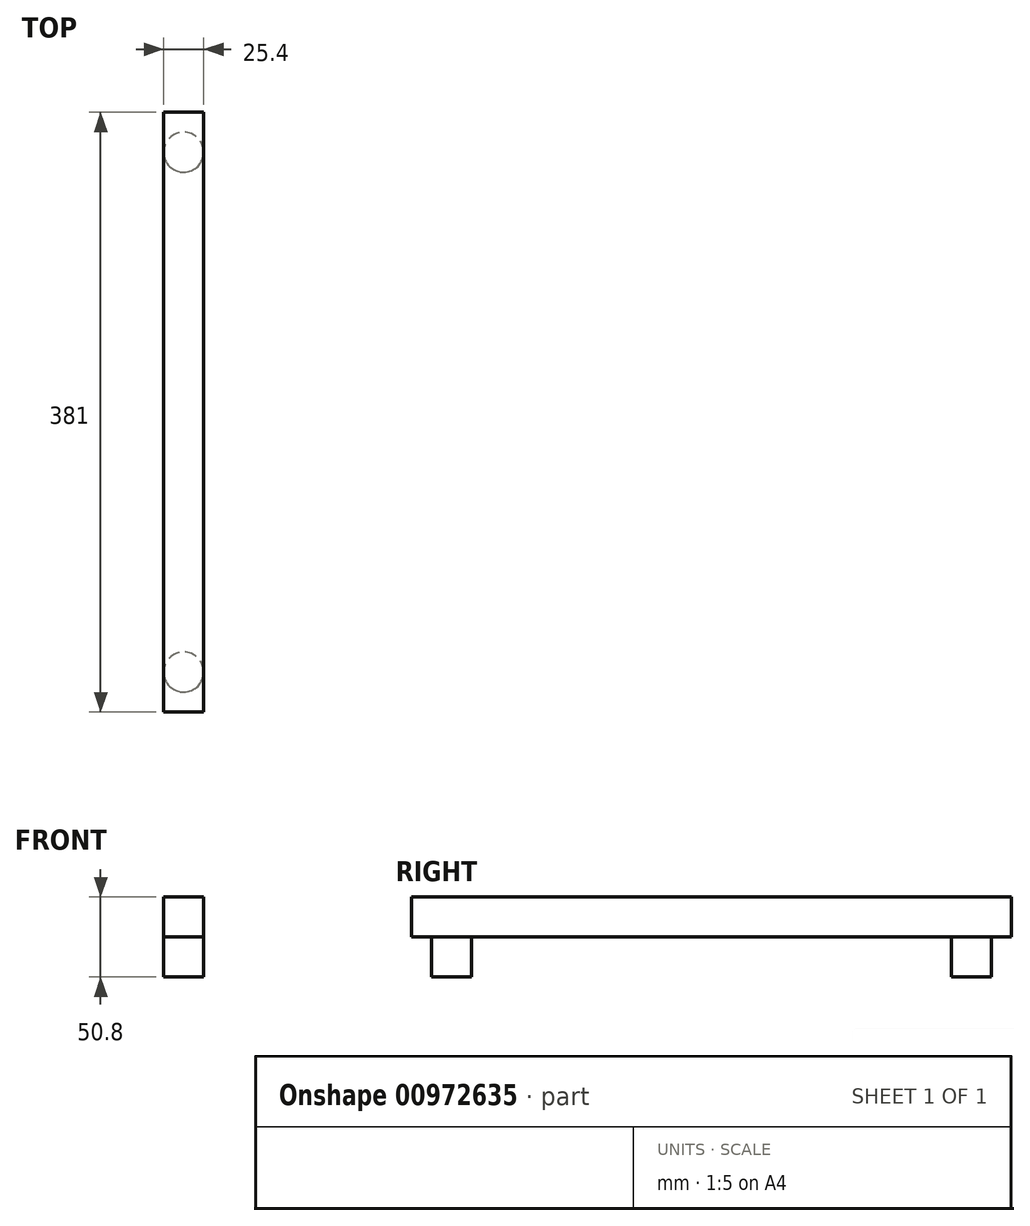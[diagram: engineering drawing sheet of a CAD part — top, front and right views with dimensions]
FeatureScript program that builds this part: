
annotation { "Feature Type Name" : "Feature", "Feature Type Description" : "" }
export const myFeature = defineFeature(function(context is Context, id is Id, definition is map)
    precondition{}
    {
        {
            var Q0;
            Q0=qCreatedBy(makeId("Top.planeOp"),FACE);
            var sketch = newSketch(context, id + "F0", { "sketchPlane" : qUnion([Q0])});
            skCircle(sketch, "E0", {"center": v(-130.07, -20.03) * mm, "radius": 12.7 * mm});
            skSolve(sketch);
        }
        {
            var Q0;
            Q0=makeQuery(id+"F0.imprint","IMPRINT",FACE,{"disambiguationData":[TD([[makeQuery(id+"F0.imprint","IMPRINT",EDGE,{"derivedFrom":sQuery(id+"F0.wireOp",EDGE,"E0")}),1.0]])]});
            extrude(context, id + "F1", {"entities" : qUnion([Q0]), "depth" : 25.4 * mm, "offsetDistance" : 25.4 * mm});
        }
        {
            var Q0;
            Q0=makeQuery(id+"F1.opExtrude","SWEPT_BODY",BODY,{"disambiguationData":[OSD([sQuery(id+"F0.wireOp",EDGE,"E0")])]});
            deleteBodies(context, id + "F2", {"entities" : qUnion([Q0])});
        }
        {
            var Q0;
            Q0=qCreatedBy(makeId("Top.planeOp"),FACE);
            var sketch = newSketch(context, id + "F3", { "sketchPlane" : qUnion([Q0])});
            skLineSegment(sketch, "E1.bottom", {"start": v(-57.57, 349.57) * mm, "end": v(-32.17, 349.57) * mm});
            skLineSegment(sketch, "E1.top", {"start": v(-57.57, -31.43) * mm, "end": v(-32.17, -31.43) * mm});
            skLineSegment(sketch, "E1.left", {"start": v(-57.57, 349.57) * mm, "end": v(-57.57, -31.43) * mm});
            skLineSegment(sketch, "E1.right", {"start": v(-32.17, 349.57) * mm, "end": v(-32.17, -31.43) * mm});
            skSolve(sketch);
        }
        {
            var Q0;
            Q0=makeQuery(id+"F3.imprint","IMPRINT",FACE,{"disambiguationData":[TD([[makeQuery(id+"F3.imprint","IMPRINT",EDGE,{"derivedFrom":sQuery(id+"F3.wireOp",EDGE,"E1.bottom")}),-1.0]])]});
            extrude(context, id + "F4", {"entities" : qUnion([Q0]), "depth" : 25.4 * mm, "offsetDistance" : 25.4 * mm});
        }
        {
            var Q0;
            Q0=makeQuery(id+"F4.opExtrude","CAP_FACE",FACE,{"disambiguationData":[OSD([sQuery(id+"F3.wireOp",EDGE,"E1.bottom"),sQuery(id+"F3.wireOp",EDGE,"E1.top"),sQuery(id+"F3.wireOp",EDGE,"E1.left"),sQuery(id+"F3.wireOp",EDGE,"E1.right")])],"isStart":true});
            var sketch = newSketch(context, id + "F5", { "sketchPlane" : qUnion([Q0])});
            skLineSegment(sketch, "E2.bottom", {"start": v(-57.57, 31.43) * mm, "end": v(-32.17, 31.43) * mm});
            skLineSegment(sketch, "E2.top", {"start": v(-57.57, 18.73) * mm, "end": v(-32.17, 18.73) * mm});
            skLineSegment(sketch, "E2.left", {"start": v(-57.57, 31.43) * mm, "end": v(-57.57, 18.73) * mm});
            skLineSegment(sketch, "E2.right", {"start": v(-32.17, 31.43) * mm, "end": v(-32.17, 18.73) * mm});
            skLineSegment(sketch, "E3.top", {"start": v(-57.57, -6.67) * mm, "end": v(-32.17, -6.67) * mm});
            skLineSegment(sketch, "E3.left", {"start": v(-57.57, 18.73) * mm, "end": v(-57.57, -6.67) * mm});
            skLineSegment(sketch, "E3.right", {"start": v(-32.17, 18.73) * mm, "end": v(-32.17, -6.67) * mm});
            skLineSegment(sketch, "E4", {"start": v(-57.57, 18.73) * mm, "end": v(-32.17, -6.67) * mm});
            skCircle(sketch, "E5", {"center": v(-44.87, 6.03) * mm, "radius": 12.7 * mm});
            skSolve(sketch);
        }
        {
            var Q0;
            {var subQ0=sQuery(id+"F5.wireOp",EDGE,"E5");var subQ1=sQuery(id+"F5.wireOp",EDGE,"E4");var subQ2=makeQuery(id+"F5.imprint","INTERSECT",VERTEX,{"disambiguationData":[OD(0.0)],"derivedFrom":[subQ1,subQ0]});Q0=makeQuery(id+"F5.imprint","IMPRINT",FACE,{"disambiguationData":[TD([[makeQuery(id+"F5.imprint","IMPRINT",EDGE,{"disambiguationData":[TD([[subQ2,-1.0]])],"derivedFrom":subQ1}),1.0]])]});}
            var Q1;
            {var subQ0=sQuery(id+"F5.wireOp",EDGE,"E5");var subQ1=sQuery(id+"F5.wireOp",EDGE,"E4");var subQ2=makeQuery(id+"F5.imprint","INTERSECT",VERTEX,{"disambiguationData":[OD(0.0)],"derivedFrom":[subQ1,subQ0]});Q1=makeQuery(id+"F5.imprint","IMPRINT",FACE,{"disambiguationData":[TD([[makeQuery(id+"F5.imprint","IMPRINT",EDGE,{"disambiguationData":[TD([[subQ2,-1.0]])],"derivedFrom":subQ1}),-1.0]])]});}
            extrude(context, id + "F6", {"entities" : qUnion([Q0, Q1]), "operationType" : NewBodyOperationType.ADD, "depth" : 50.8 * mm, "offsetDistance" : 25.4 * mm});
        }
        {
            var Q0;
            Q0=makeQuery(id+"F6.opExtrude","CAP_FACE",FACE,{"disambiguationData":[OSD([sQuery(id+"F5.wireOp",EDGE,"E5")])],"isStart":false});
            extrude(context, id + "F7", {"entities" : qUnion([Q0]), "operationType" : NewBodyOperationType.REMOVE, "oppositeDirection" : true, "depth" : 25.4 * mm, "offsetDistance" : 25.4 * mm});
        }
        {
            var Q0;
            {var subQ0=sQuery(id+"F3.wireOp",EDGE,"E1.left");var subQ1=sQuery(id+"F3.wireOp",EDGE,"E1.right");var subQ2=sQuery(id+"F3.wireOp",EDGE,"E1.bottom");var subQ3=makeQuery(id+"F4.opExtrude","CAP_FACE",FACE,{"disambiguationData":[OSD([subQ2,sQuery(id+"F3.wireOp",EDGE,"E1.top"),subQ0,subQ1])],"isStart":true});Q0=makeQuery(id+"F6.boolean.opBoolean","SPLIT",FACE,{"disambiguationData":[TD([makeQuery(id+"F4.opExtrude","SWEPT_FACE",FACE,{"disambiguationData":[OSD([subQ2])]})])],"derivedFrom":subQ3});}
            var sketch = newSketch(context, id + "F8", { "sketchPlane" : qUnion([Q0])});
            skLineSegment(sketch, "E6.bottom", {"start": v(-57.57, -349.57) * mm, "end": v(-32.17, -349.57) * mm});
            skLineSegment(sketch, "E6.top", {"start": v(-57.57, -336.87) * mm, "end": v(-32.17, -336.87) * mm});
            skLineSegment(sketch, "E6.left", {"start": v(-57.57, -349.57) * mm, "end": v(-57.57, -336.87) * mm});
            skLineSegment(sketch, "E6.right", {"start": v(-32.17, -349.57) * mm, "end": v(-32.17, -336.87) * mm});
            skLineSegment(sketch, "E7.top", {"start": v(-57.57, -311.47) * mm, "end": v(-32.17, -311.47) * mm});
            skLineSegment(sketch, "E7.left", {"start": v(-57.57, -336.87) * mm, "end": v(-57.57, -311.47) * mm});
            skLineSegment(sketch, "E7.right", {"start": v(-32.17, -336.87) * mm, "end": v(-32.17, -311.47) * mm});
            skLineSegment(sketch, "E8", {"start": v(-57.57, -311.47) * mm, "end": v(-32.17, -336.87) * mm});
            skCircle(sketch, "E9", {"center": v(-44.87, -324.17) * mm, "radius": 12.7 * mm});
            skSolve(sketch);
        }
        {
            var Q0;
            {var subQ0=sQuery(id+"F8.wireOp",EDGE,"E9");var subQ1=sQuery(id+"F8.wireOp",EDGE,"E8");var subQ2=makeQuery(id+"F8.imprint","INTERSECT",VERTEX,{"disambiguationData":[OD(0.0)],"derivedFrom":[subQ1,subQ0]});Q0=makeQuery(id+"F8.imprint","IMPRINT",FACE,{"disambiguationData":[TD([[makeQuery(id+"F8.imprint","IMPRINT",EDGE,{"disambiguationData":[TD([[subQ2,-1.0]])],"derivedFrom":subQ1}),1.0]])]});}
            var Q1;
            {var subQ0=sQuery(id+"F8.wireOp",EDGE,"E9");var subQ1=sQuery(id+"F8.wireOp",EDGE,"E8");var subQ2=makeQuery(id+"F8.imprint","INTERSECT",VERTEX,{"disambiguationData":[OD(0.0)],"derivedFrom":[subQ1,subQ0]});Q1=makeQuery(id+"F8.imprint","IMPRINT",FACE,{"disambiguationData":[TD([[makeQuery(id+"F8.imprint","IMPRINT",EDGE,{"disambiguationData":[TD([[subQ2,-1.0]])],"derivedFrom":subQ1}),-1.0]])]});}
            extrude(context, id + "F9", {"entities" : qUnion([Q0, Q1]), "operationType" : NewBodyOperationType.ADD, "depth" : 25.4 * mm, "offsetDistance" : 25.4 * mm});
        }
    });
